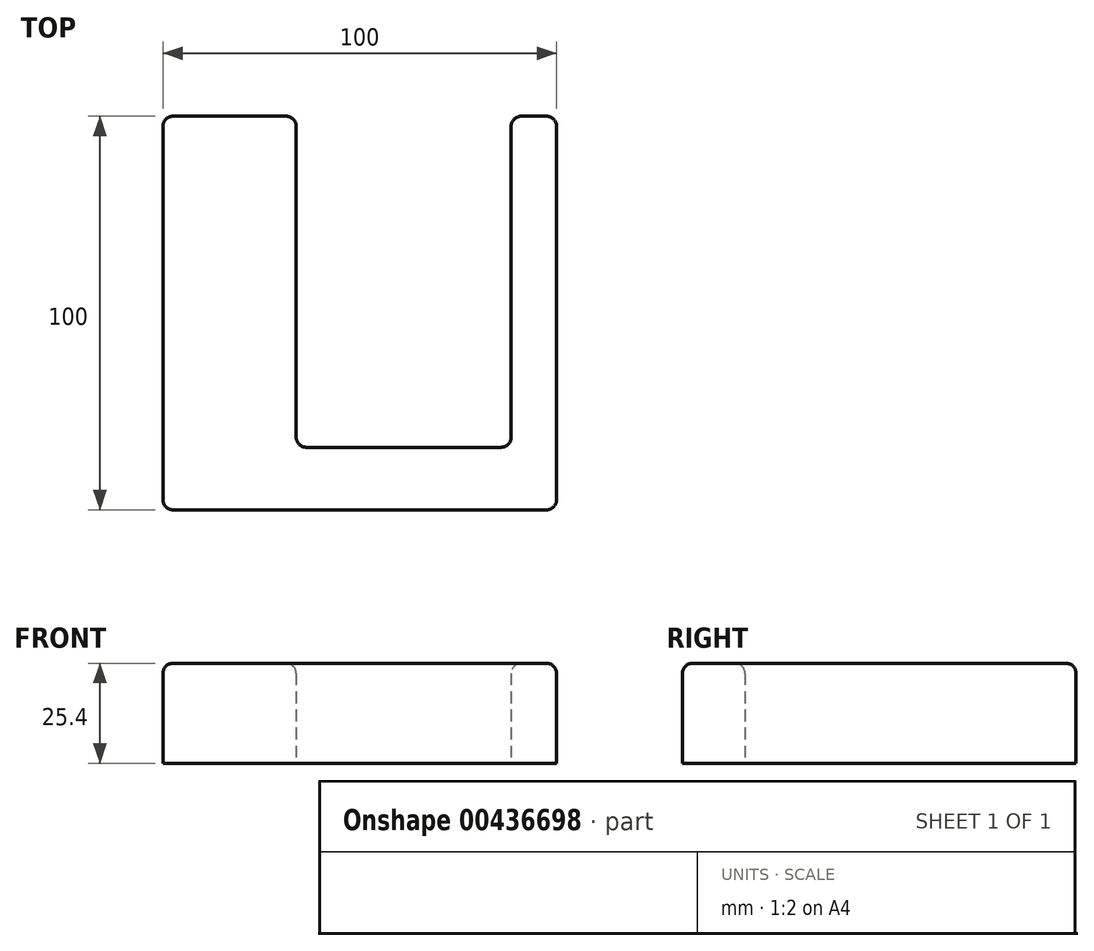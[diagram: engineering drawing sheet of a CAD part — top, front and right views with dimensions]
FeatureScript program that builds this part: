
annotation { "Feature Type Name" : "Feature", "Feature Type Description" : "" }
export const myFeature = defineFeature(function(context is Context, id is Id, definition is map)
    precondition{}
    {
        {
            var Q0;
            Q0=qCreatedBy(makeId("Top.planeOp"),FACE);
            var sketch = newSketch(context, id + "F0", { "sketchPlane" : qUnion([Q0])});
            skLineSegment(sketch, "E0.bottom", {"start": v(-93.01, -34.81) * mm, "end": v(6.99, -34.81) * mm});
            skLineSegment(sketch, "E0.top", {"start": v(-93.01, 65.19) * mm, "end": v(6.99, 65.19) * mm});
            skLineSegment(sketch, "E0.left", {"start": v(-93.01, -34.81) * mm, "end": v(-93.01, 65.19) * mm});
            skLineSegment(sketch, "E0.right", {"start": v(6.99, -34.81) * mm, "end": v(6.99, 65.19) * mm});
            skLineSegment(sketch, "E1.bottom", {"start": v(-59.14, 65.19) * mm, "end": v(-4.52, 65.19) * mm});
            skLineSegment(sketch, "E1.top", {"start": v(-59.14, -18.92) * mm, "end": v(-4.52, -18.92) * mm});
            skLineSegment(sketch, "E1.left", {"start": v(-59.14, 65.19) * mm, "end": v(-59.14, -18.92) * mm});
            skLineSegment(sketch, "E1.right", {"start": v(-4.52, 65.19) * mm, "end": v(-4.52, -18.92) * mm});
            skSolve(sketch);
        }
        {
            var Q0;
            Q0=makeQuery(id+"F0.imprint","IMPRINT",FACE,{"disambiguationData":[TD([[makeQuery(id+"F0.imprint","IMPRINT",EDGE,{"derivedFrom":sQuery(id+"F0.wireOp",EDGE,"E0.bottom")}),1.0]])]});
            extrude(context, id + "F1", {"entities" : qUnion([Q0]), "depth" : 25.4 * mm});
        }
        {
            var Q0;
            Q0=makeQuery(id+"F1.opExtrude","SWEPT_EDGE",EDGE,{"disambiguationData":[OSD([sQuery(id+"F0.wireOp",EDGE,"E0.bottom"),sQuery(id+"F0.wireOp",EDGE,"E0.left")])]});
            var Q1;
            Q1=makeQuery(id+"F1.opExtrude","SWEPT_EDGE",EDGE,{"disambiguationData":[OSD([sQuery(id+"F0.wireOp",EDGE,"E0.bottom"),sQuery(id+"F0.wireOp",EDGE,"E0.right")])]});
            var Q2;
            Q2=makeQuery(id+"F1.opExtrude","SWEPT_EDGE",EDGE,{"disambiguationData":[OSD([sQuery(id+"F0.wireOp",EDGE,"E1.top"),sQuery(id+"F0.wireOp",EDGE,"E1.right")])]});
            var Q3;
            Q3=makeQuery(id+"F1.opExtrude","SWEPT_EDGE",EDGE,{"disambiguationData":[OSD([sQuery(id+"F0.wireOp",EDGE,"E1.top"),sQuery(id+"F0.wireOp",EDGE,"E1.left")])]});
            var Q4;
            Q4=makeQuery(id+"F1.opExtrude","SWEPT_EDGE",EDGE,{"disambiguationData":[OSD([sQuery(id+"F0.wireOp",EDGE,"E0.top"),sQuery(id+"F0.wireOp",EDGE,"E1.bottom"),sQuery(id+"F0.wireOp",EDGE,"E1.left")])]});
            var Q5;
            Q5=makeQuery(id+"F1.opExtrude","SWEPT_EDGE",EDGE,{"disambiguationData":[OSD([sQuery(id+"F0.wireOp",EDGE,"E0.top"),sQuery(id+"F0.wireOp",EDGE,"E0.left")])]});
            var Q6;
            Q6=makeQuery(id+"F1.opExtrude","SWEPT_EDGE",EDGE,{"disambiguationData":[OSD([sQuery(id+"F0.wireOp",EDGE,"E0.top"),sQuery(id+"F0.wireOp",EDGE,"E0.right")])]});
            var Q7;
            Q7=makeQuery(id+"F1.opExtrude","SWEPT_EDGE",EDGE,{"disambiguationData":[OSD([sQuery(id+"F0.wireOp",EDGE,"E0.top"),sQuery(id+"F0.wireOp",EDGE,"E1.bottom"),sQuery(id+"F0.wireOp",EDGE,"E1.right")])]});
            fillet(context, id + "F2", {"entities" : qUnion([Q0, Q1, Q2, Q3, Q4, Q5, Q6, Q7]), "radius" : 2.54 * mm, "tangentPropagation" : true, "allowEdgeOverflow" : false});
        }
        {
            var Q0;
            Q0=makeQuery(id+"F1.opExtrude","CAP_FACE",FACE,{"disambiguationData":[OSD([sQuery(id+"F0.wireOp",EDGE,"E0.bottom"),sQuery(id+"F0.wireOp",EDGE,"E0.top"),sQuery(id+"F0.wireOp",EDGE,"E0.left"),sQuery(id+"F0.wireOp",EDGE,"E0.right"),sQuery(id+"F0.wireOp",EDGE,"E1.top"),sQuery(id+"F0.wireOp",EDGE,"E1.left"),sQuery(id+"F0.wireOp",EDGE,"E1.right")])],"isStart":false});
            fillet(context, id + "F3", {"entities" : qUnion([Q0]), "radius" : 2.54 * mm, "tangentPropagation" : true, "allowEdgeOverflow" : false});
        }
    });
